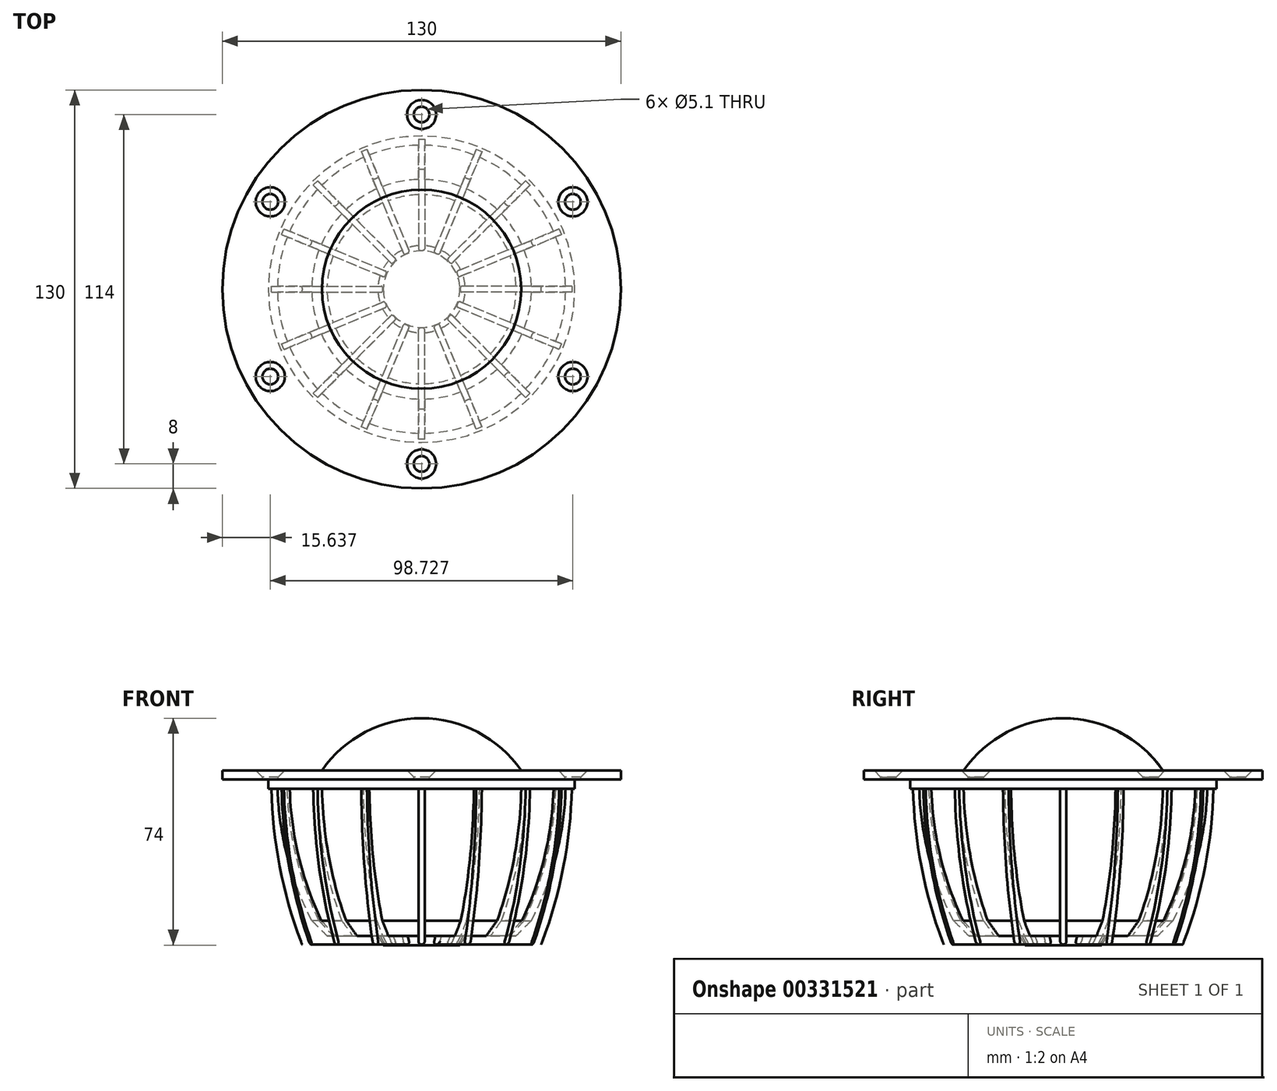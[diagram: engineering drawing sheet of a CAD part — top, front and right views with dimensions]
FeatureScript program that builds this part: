
annotation { "Feature Type Name" : "Feature", "Feature Type Description" : "" }
export const myFeature = defineFeature(function(context is Context, id is Id, definition is map)
    precondition{}
    {
        {
            var Q0;
            Q0=qCreatedBy(makeId("Right.planeOp"),FACE);
            var sketch = newSketch(context, id + "F0", { "sketchPlane" : qUnion([Q0])});
            skLineSegment(sketch, "E0", {"start": v(0, 0) * mm, "end": v(0, 34) * mm, "construction": true});
            skLineSegment(sketch, "E1", {"start": v(32.5, 0) * mm, "end": v(65, 0) * mm});
            skLineSegment(sketch, "E2", {"start": v(65, 0) * mm, "end": v(65, -3) * mm});
            skLineSegment(sketch, "E3", {"start": v(65, -3) * mm, "end": v(50, -3) * mm});
            skArc(sketch, "E4", {"start": v(0, 17) * mm, "mid": v(18.34, 12.5) * mm, "end": v(32.5, 0) * mm});
            skLineSegment(sketch, "E5", {"start": v(50, -3) * mm, "end": v(50, -6) * mm});
            skLineSegment(sketch, "E6", {"start": v(50, -6) * mm, "end": v(47, -6) * mm});
            skArc(sketch, "E7", {"start": v(47, -6) * mm, "mid": v(43.84, -28.13) * mm, "end": v(35.84, -49) * mm});
            skLineSegment(sketch, "E8", {"start": v(35.84, -49) * mm, "end": v(30.84, -54) * mm});
            skLineSegment(sketch, "E9", {"start": v(30.84, -54) * mm, "end": v(14.23, -54) * mm});
            skLineSegment(sketch, "E10", {"start": v(14.23, -54) * mm, "end": v(12.5, -57) * mm});
            skLineSegment(sketch, "E11", {"start": v(12.5, -57) * mm, "end": v(0, -57) * mm});
            skLineSegment(sketch, "E12", {"start": v(0, -57) * mm, "end": v(0, 17) * mm});
            skSolve(sketch);
        }
        {
            var Q0;
            Q0 = qSketchRegion(id + "F0", true);
            var Q1;
            Q1=sQuery(id+"F0.wireOp",EDGE,"E0");
            revolve(context, id + "F1", {"entities" : qUnion([Q0]), "axis" : qUnion([Q1]), "revolveType" : RevolveType.FULL});
        }
        {
            var Q0;
            Q0=makeQuery(id+"F1.opRevolve","SWEPT_FACE",FACE,{"disambiguationData":[OSD([sQuery(id+"F0.wireOp",EDGE,"E6")])]});
            var sketch = newSketch(context, id + "F2", { "sketchPlane" : qUnion([Q0])});
            skLineSegment(sketch, "E13", {"start": v(0, 0) * mm, "end": v(0, -49) * mm, "construction": true});
            skLineSegment(sketch, "E14", {"start": v(0, -49) * mm, "end": v(1, -49) * mm});
            skLineSegment(sketch, "E15", {"start": v(1, -49) * mm, "end": v(1, -10) * mm});
            skLineSegment(sketch, "E16", {"start": v(1, -10) * mm, "end": v(0, -10) * mm});
            skLineSegment(sketch, "E17.MirrorCS", {"start": v(-1, -10) * mm, "end": v(0, -10) * mm});
            skLineSegment(sketch, "E18.MirrorCS", {"start": v(-1, -49) * mm, "end": v(-1, -10) * mm});
            skLineSegment(sketch, "E19.MirrorCS", {"start": v(0, -49) * mm, "end": v(-1, -49) * mm});
            skPoint(sketch, "E20", {"position": v(0, -50) * mm});
            skSolve(sketch);
        }
        {
            var Q0;
            Q0 = qSketchRegion(id + "F2", true);
            extrude(context, id + "F3", {"entities" : qUnion([Q0]), "depth" : 50.8 * mm});
        }
        {
            var Q0;
            Q0=makeQuery(id+"F3.opExtrude","SWEPT_FACE",FACE,{"disambiguationData":[OSD([sQuery(id+"F2.wireOp",EDGE,"E18.MirrorCS")])]});
            var sketch = newSketch(context, id + "F4", { "sketchPlane" : qUnion([Q0])});
            skArc(sketch, "E21", {"start": v(-49, -6) * mm, "mid": v(-46.22, -31.84) * mm, "end": v(-39, -56.8) * mm});
            skLineSegment(sketch, "E22", {"start": v(-39, -56.8) * mm, "end": v(-49, -56.8) * mm});
            skLineSegment(sketch, "E23", {"start": v(-49, -56.8) * mm, "end": v(-49, -6) * mm});
            skSolve(sketch);
        }
        {
            var Q0;
            Q0 = qSketchRegion(id + "F4", true);
            extrude(context, id + "F5", {"entities" : qUnion([Q0]), "operationType" : NewBodyOperationType.REMOVE, "endBound" : BoundingType.UP_TO_NEXT, "oppositeDirection" : true, "depth" : 25 * mm});
        }
        {
            var Q0;
            Q0=makeQuery(id+"F5.boolean.opBoolean","COPY",EDGE,{"derivedFrom":makeQuery(id+"F5.opExtrude","SWEPT_EDGE",EDGE,{"disambiguationData":[OSD([sQuery(id+"F2.wireOp",EDGE,"E18.MirrorCS"),sQuery(id+"F4.wireOp",EDGE,"E21"),sQuery(id+"F4.wireOp",EDGE,"E22")])]})});
            var Q1;
            Q1=makeQuery(id+"F5.boolean.opBoolean","COPY",EDGE,{"derivedFrom":makeQuery(id+"F5.opExtrude","CAP_EDGE",EDGE,{"disambiguationData":[OSD([sQuery(id+"F4.wireOp",EDGE,"E21")])],"isStart":true})});
            var Q2;
            Q2=makeQuery(id+"F3.opExtrude","CAP_EDGE",EDGE,{"disambiguationData":[OSD([sQuery(id+"F2.wireOp",EDGE,"E18.MirrorCS")])],"isStart":false});
            var Q3;
            Q3=makeQuery(id+"F3.opExtrude","CAP_EDGE",EDGE,{"disambiguationData":[OSD([sQuery(id+"F2.wireOp",EDGE,"E15")])],"isStart":false});
            var Q4;
            Q4=makeQuery(id+"F5.boolean.opBoolean","COPY",EDGE,{"derivedFrom":makeQuery(id+"F5.opExtrude","TWEAK_EDGE",EDGE,{"derivedFrom":[makeQuery(id+"F3.opExtrude","SWEPT_FACE",FACE,{"disambiguationData":[OSD([sQuery(id+"F2.wireOp",EDGE,"E15")])]}),makeQuery(id+"F4.imprint","IMPRINT",EDGE,{"derivedFrom":sQuery(id+"F4.wireOp",EDGE,"E21")})]})});
            fillet(context, id + "F6", {"entities" : qUnion([Q0, Q1, Q2, Q3, Q4]), "radius" : 1 * mm, "tangentPropagation" : true, "allowEdgeOverflow" : false});
        }
        {
            var Q0;
            Q0=makeQuery(id+"F3.opExtrude","SWEPT_BODY",BODY,{"disambiguationData":[OSD([sQuery(id+"F2.wireOp",EDGE,"E14"),sQuery(id+"F2.wireOp",EDGE,"E15"),sQuery(id+"F2.wireOp",EDGE,"E16"),sQuery(id+"F2.wireOp",EDGE,"E17.MirrorCS"),sQuery(id+"F2.wireOp",EDGE,"E18.MirrorCS"),sQuery(id+"F2.wireOp",EDGE,"E19.MirrorCS")])]});
            var Q1;
            Q1=sQuery(id+"F0.wireOp",EDGE,"E12");
            circularPattern(context, id + "F7", {"operationType" : NewBodyOperationType.ADD, "entities" : qUnion([Q0]), "axis" : qUnion([Q1]), "angle" : 360 * degree, "instanceCount" : 16, "equalSpace" : true});
        }
        {
            var Q0;
            Q0=makeQuery(id+"F1.opRevolve","SWEPT_FACE",FACE,{"disambiguationData":[OSD([sQuery(id+"F0.wireOp",EDGE,"E1")])]});
            var sketch = newSketch(context, id + "F8", { "sketchPlane" : qUnion([Q0])});
            skPoint(sketch, "E24", {"position": v(0, 57) * mm});
            skPoint(sketch, "E25.1.0", {"position": v(-49.36, -28.5) * mm});
            skPoint(sketch, "E25.2.0", {"position": v(49.36, -28.5) * mm});
            skPoint(sketch, "E25.center", {"position": v(0, 0) * mm});
            skPoint(sketch, "E26.1.0", {"position": v(-49.36, 28.5) * mm});
            skPoint(sketch, "E27.0.3.0", {"position": v(0, -57) * mm});
            skPoint(sketch, "E27.0.5.0", {"position": v(49.36, 28.5) * mm});
            skSolve(sketch);
        }
        {
            var Q0;
            Q0=sQuery(id+"F8.wireOp",VERTEX,"E24");
            var Q1;
            Q1=sQuery(id+"F8.wireOp",VERTEX,"E27.0.5.0");
            var Q2;
            Q2=sQuery(id+"F8.wireOp",VERTEX,"E25.2.0");
            var Q3;
            Q3=sQuery(id+"F8.wireOp",VERTEX,"E27.0.3.0");
            var Q4;
            Q4=sQuery(id+"F8.wireOp",VERTEX,"E25.1.0");
            var Q5;
            Q5=sQuery(id+"F8.wireOp",VERTEX,"E26.1.0");
            var Q6;
            Q6=makeQuery(id+"F1.opRevolve","SWEPT_BODY",BODY,{"disambiguationData":[OSD([sQuery(id+"F0.wireOp",EDGE,"E1"),sQuery(id+"F0.wireOp",EDGE,"E2"),sQuery(id+"F0.wireOp",EDGE,"E3"),sQuery(id+"F0.wireOp",EDGE,"E4"),sQuery(id+"F0.wireOp",EDGE,"E5"),sQuery(id+"F0.wireOp",EDGE,"E6"),sQuery(id+"F0.wireOp",EDGE,"E7"),sQuery(id+"F0.wireOp",EDGE,"E8"),sQuery(id+"F0.wireOp",EDGE,"E9"),sQuery(id+"F0.wireOp",EDGE,"E10"),sQuery(id+"F0.wireOp",EDGE,"E11"),sQuery(id+"F0.wireOp",EDGE,"E12")])]});
            hole(context, id + "F9", {"style" : HoleStyle.C_SINK, "endStyle" : HoleEndStyle.BLIND, "holeDiameter" : 5.1 * mm, "cSinkDiameter" : 9.5 * mm, "cSinkAngle" : 90 * degree, "holeDepth" : 12 * mm, "tappedDepth" : 12 * mm, "tapClearance" : 3, "startFromSketch" : true, "locations" : qUnion([Q0, Q1, Q2, Q3, Q4, Q5]), "scope" : qUnion([Q6])});
        }
    });
